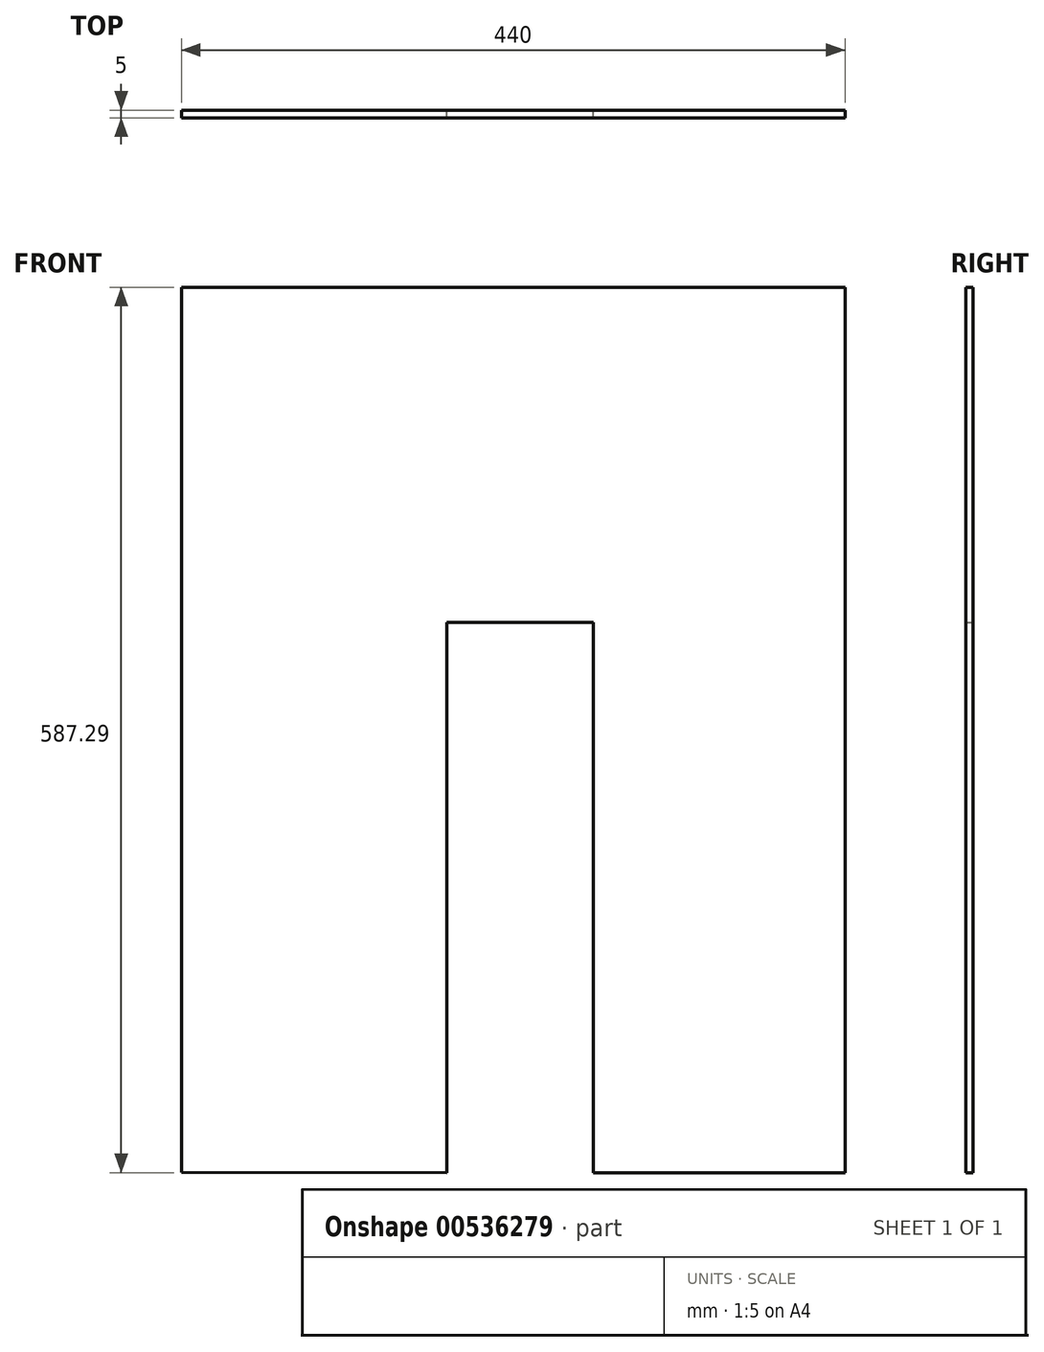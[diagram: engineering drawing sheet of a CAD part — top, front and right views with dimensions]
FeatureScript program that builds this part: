
annotation { "Feature Type Name" : "Feature", "Feature Type Description" : "" }
export const myFeature = defineFeature(function(context is Context, id is Id, definition is map)
    precondition{}
    {
        {
            var Q0;
            Q0=qCreatedBy(makeId("Front.planeOp"),FACE);
            var sketch = newSketch(context, id + "F0", { "sketchPlane" : qUnion([Q0])});
            skLineSegment(sketch, "E0", {"start": v(-54.97, -74.76) * mm, "end": v(-54.97, 512.24) * mm});
            skLineSegment(sketch, "E1", {"start": v(-54.97, 512.24) * mm, "end": v(385.03, 512.24) * mm});
            skLineSegment(sketch, "E2", {"start": v(385.03, 512.24) * mm, "end": v(385.03, -75.05) * mm});
            skLineSegment(sketch, "E3", {"start": v(385.03, -75.05) * mm, "end": v(218.03, -75.05) * mm});
            skLineSegment(sketch, "E4", {"start": v(218.03, -75.05) * mm, "end": v(218.03, 289.95) * mm});
            skLineSegment(sketch, "E5", {"start": v(218.03, 289.95) * mm, "end": v(121.03, 289.95) * mm});
            skLineSegment(sketch, "E6", {"start": v(121.03, 289.95) * mm, "end": v(121.03, -75.05) * mm});
            skLineSegment(sketch, "E7", {"start": v(121.03, -75.05) * mm, "end": v(-54.97, -74.76) * mm});
            skSolve(sketch);
        }
        {
            var Q0;
            Q0=makeQuery(id+"F0.imprint","IMPRINT",FACE,{"disambiguationData":[TD([[makeQuery(id+"F0.imprint","IMPRINT",EDGE,{"derivedFrom":sQuery(id+"F0.wireOp",EDGE,"E0")}),-1.0]])]});
            extrude(context, id + "F1", {"entities" : qUnion([Q0]), "depth" : 5 * mm, "offsetDistance" : 25 * mm});
        }
    });
